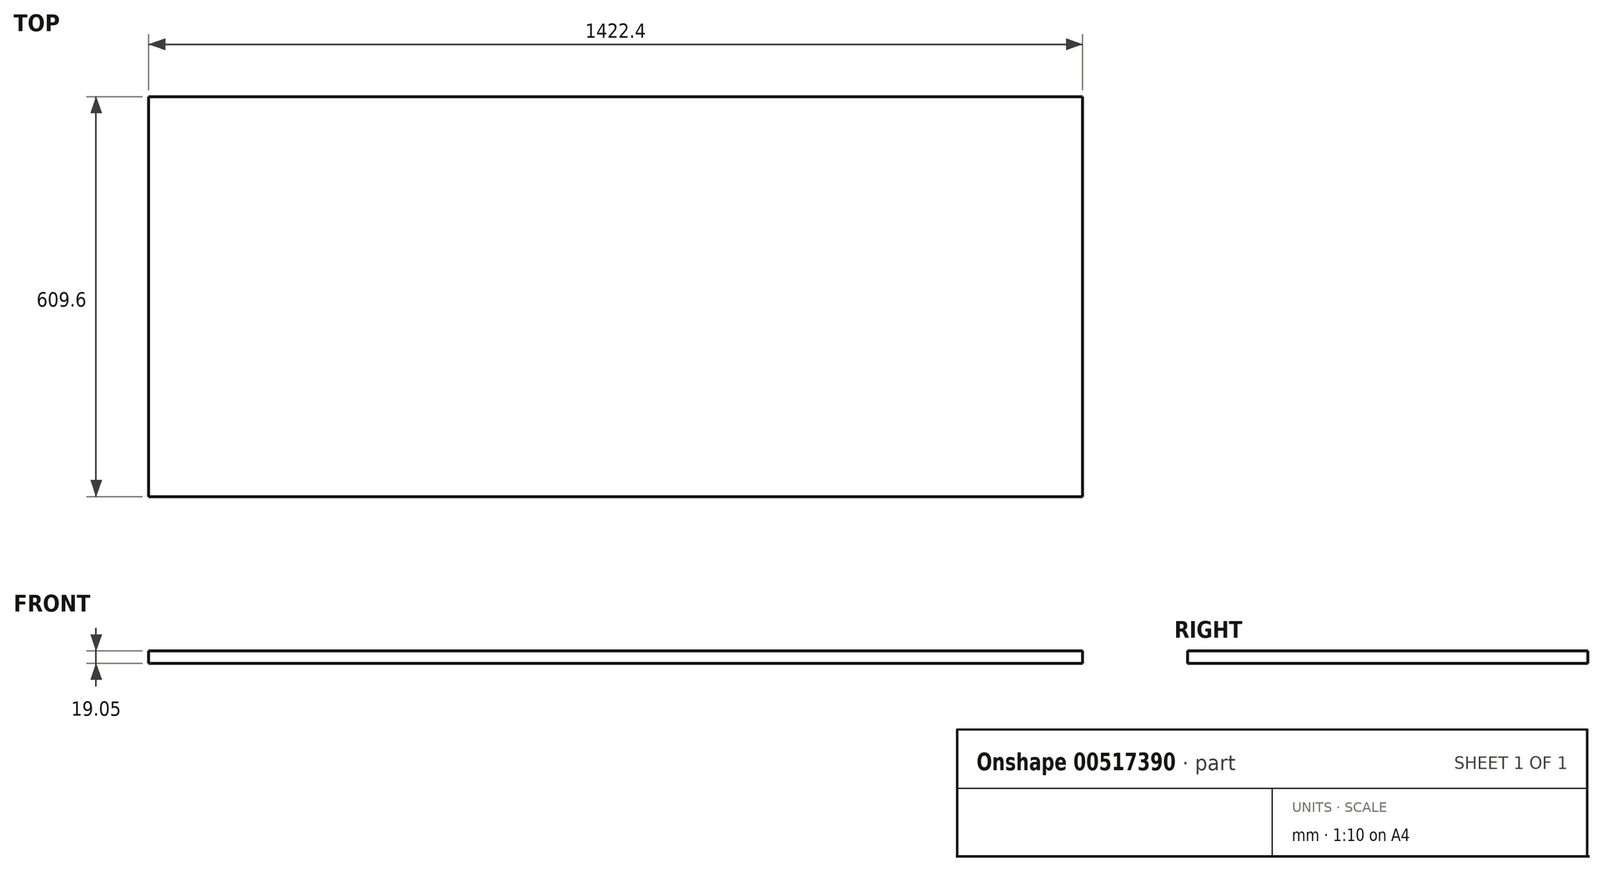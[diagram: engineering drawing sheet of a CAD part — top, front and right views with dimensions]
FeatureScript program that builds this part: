
annotation { "Feature Type Name" : "Feature", "Feature Type Description" : "" }
export const myFeature = defineFeature(function(context is Context, id is Id, definition is map)
    precondition{}
    {
        {
            var Q0;
            Q0=qCreatedBy(makeId("Top.planeOp"),FACE);
            var sketch = newSketch(context, id + "F0", { "sketchPlane" : qUnion([Q0])});
            skLineSegment(sketch, "E0.bottom", {"start": v(-711.2, -304.8) * mm, "end": v(711.2, -304.8) * mm});
            skLineSegment(sketch, "E0.top", {"start": v(-711.2, 304.8) * mm, "end": v(711.2, 304.8) * mm});
            skLineSegment(sketch, "E0.left", {"start": v(-711.2, -304.8) * mm, "end": v(-711.2, 304.8) * mm});
            skLineSegment(sketch, "E0.right", {"start": v(711.2, -304.8) * mm, "end": v(711.2, 304.8) * mm});
            skPoint(sketch, "E0.middle", {"position": v(0, 0) * mm});
            skSolve(sketch);
        }
        {
            var Q0;
            Q0 = qSketchRegion(id + "F0", true);
            extrude(context, id + "F1", {"entities" : qUnion([Q0]), "depth" : 19.05 * mm});
        }
    });
